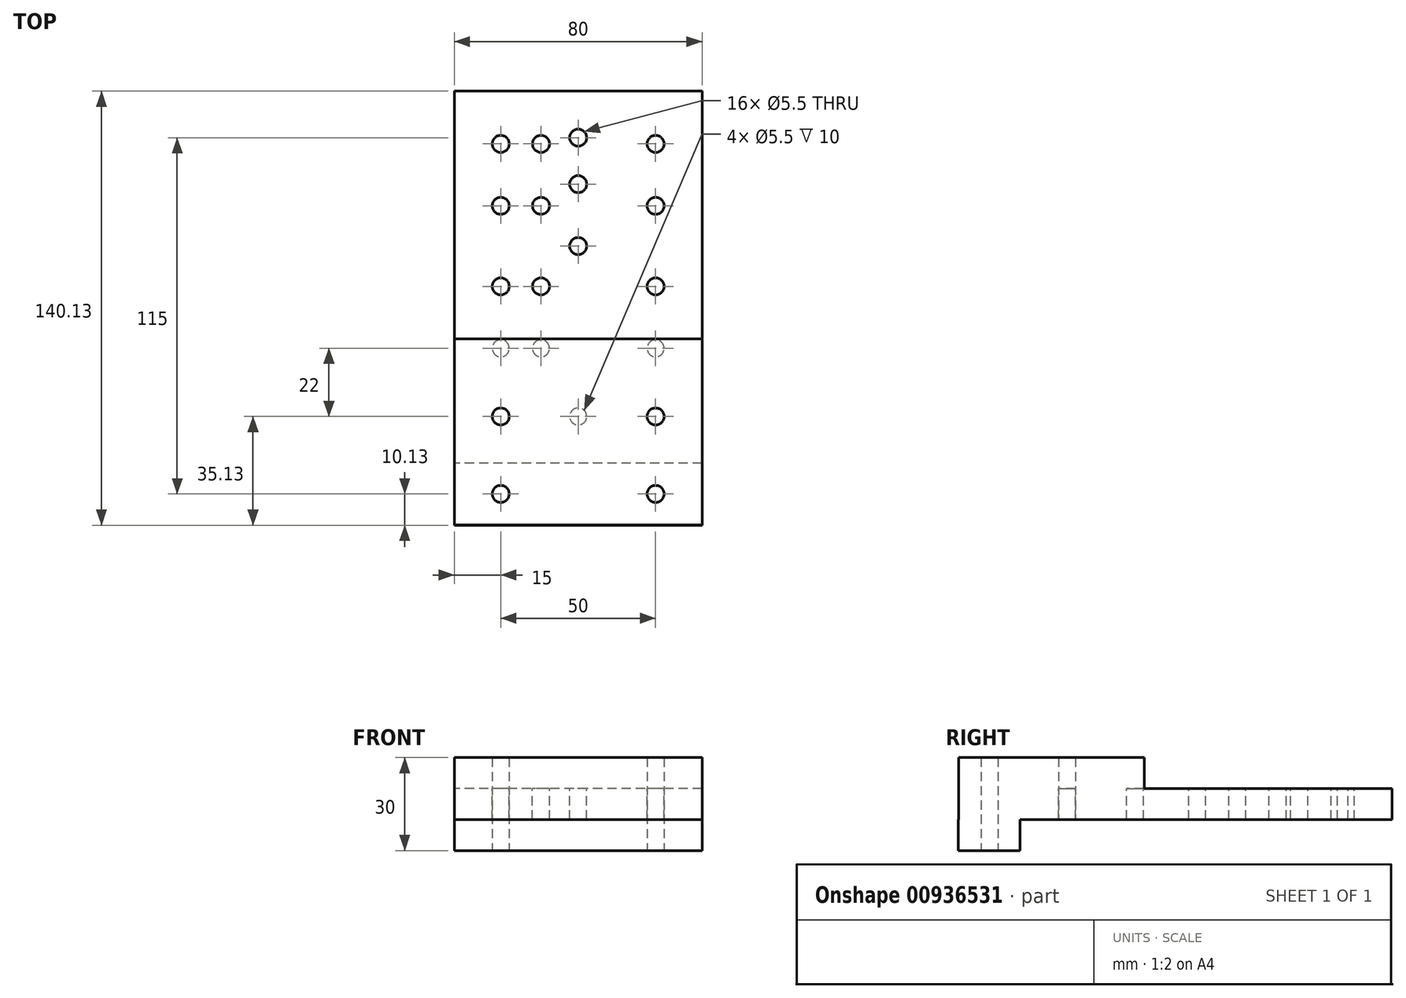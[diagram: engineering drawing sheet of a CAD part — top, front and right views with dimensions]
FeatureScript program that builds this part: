
annotation { "Feature Type Name" : "Feature", "Feature Type Description" : "" }
export const myFeature = defineFeature(function(context is Context, id is Id, definition is map)
    precondition{}
    {
        {
            var Q0;
            Q0=qCreatedBy(makeId("Top.planeOp"),FACE);
            var sketch = newSketch(context, id + "F0", { "sketchPlane" : qUnion([Q0])});
            skLineSegment(sketch, "E0.bottom", {"start": v(40, 70) * mm, "end": v(-40, 70) * mm});
            skLineSegment(sketch, "E0.top", {"start": v(40, -70) * mm, "end": v(-40, -70) * mm});
            skLineSegment(sketch, "E0.left", {"start": v(40, 70) * mm, "end": v(40, -70) * mm});
            skLineSegment(sketch, "E0.right", {"start": v(-40, 70) * mm, "end": v(-40, -70) * mm});
            skPoint(sketch, "E0.middle", {"position": v(0, 0) * mm});
            skLineSegment(sketch, "E1", {"start": v(-40, 30) * mm, "end": v(40, 30) * mm, "construction": true});
            skLineSegment(sketch, "E2", {"start": v(-40, 10) * mm, "end": v(40, 10) * mm, "construction": true});
            skPoint(sketch, "E3", {"position": v(-25, 53) * mm});
            skPoint(sketch, "E4", {"position": v(-12, 53) * mm});
            skPoint(sketch, "E5", {"position": v(25, 53) * mm});
            skPoint(sketch, "E6.MirrorP", {"position": v(-25, 7) * mm});
            skPoint(sketch, "E7.MirrorP", {"position": v(-12, 7) * mm});
            skPoint(sketch, "E8.MirrorP", {"position": v(25, 7) * mm});
            skPoint(sketch, "E9", {"position": v(-25, 33) * mm});
            skPoint(sketch, "E10", {"position": v(-12, 33) * mm});
            skPoint(sketch, "E11", {"position": v(25, 33) * mm});
            skPoint(sketch, "E12.MirrorP", {"position": v(-25, -13) * mm});
            skPoint(sketch, "E13.MirrorP", {"position": v(-12, -13) * mm});
            skPoint(sketch, "E14.MirrorP", {"position": v(25, -13) * mm});
            skPoint(sketch, "E15", {"position": v(0, -35) * mm});
            skPoint(sketch, "E16.MirrorP", {"position": v(0, 55) * mm});
            skPoint(sketch, "E17", {"position": v(0, 40) * mm});
            skPoint(sketch, "E18.MirrorP", {"position": v(0, 20) * mm});
            skSolve(sketch);
        }
        {
            var Q0;
            Q0 = qSketchRegion(id + "F0", true);
            extrude(context, id + "F1", {"entities" : qUnion([Q0]), "depth" : 10 * mm, "offsetDistance" : 25 * mm});
        }
        {
            var Q0;
            Q0=sQuery(id+"F0.wireOp",VERTEX,"E8.MirrorP");
            var Q1;
            Q1=sQuery(id+"F0.wireOp",VERTEX,"E14.MirrorP");
            var Q2;
            Q2=sQuery(id+"F0.wireOp",VERTEX,"E11");
            var Q3;
            Q3=sQuery(id+"F0.wireOp",VERTEX,"E5");
            var Q4;
            Q4=sQuery(id+"F0.wireOp",VERTEX,"E4");
            var Q5;
            Q5=sQuery(id+"F0.wireOp",VERTEX,"E10");
            var Q6;
            Q6=sQuery(id+"F0.wireOp",VERTEX,"E9");
            var Q7;
            Q7=sQuery(id+"F0.wireOp",VERTEX,"E3");
            var Q8;
            Q8=sQuery(id+"F0.wireOp",VERTEX,"E7.MirrorP");
            var Q9;
            Q9=sQuery(id+"F0.wireOp",VERTEX,"E6.MirrorP");
            var Q10;
            Q10=sQuery(id+"F0.wireOp",VERTEX,"E13.MirrorP");
            var Q11;
            Q11=sQuery(id+"F0.wireOp",VERTEX,"E12.MirrorP");
            var Q12;
            Q12=makeQuery(id+"F1.opExtrude","SWEPT_BODY",BODY,{"disambiguationData":[OSD([sQuery(id+"F0.wireOp",EDGE,"E0.bottom"),sQuery(id+"F0.wireOp",EDGE,"E0.top"),sQuery(id+"F0.wireOp",EDGE,"E0.left"),sQuery(id+"F0.wireOp",EDGE,"E0.right")])]});
            hole(context, id + "F2", {"style" : HoleStyle.SIMPLE, "endStyle" : HoleEndStyle.THROUGH, "oppositeDirection" : true, "standardTappedOrClearance" : lookupTablePath({ "fit" : "Normal", "standard" : "ISO", "size" : "M5", "type" : "Clearance" }), "standardBlindInLast" : lookupTablePath({ "fit" : "Normal", "standard" : "ISO", "engagement" : "75%", "pitch" : "0.8 mm", "size" : "M5", "type" : "Clearance & tapped" }), "holeDiameter" : 5.5 * mm, "majorDiameter" : 5 * mm, "tappedDepth" : 12 * mm, "tapClearance" : 3, "locations" : qUnion([Q0, Q1, Q2, Q3, Q4, Q5, Q6, Q7, Q8, Q9, Q10, Q11]), "scope" : qUnion([Q12]), "startStyle" : HoleStartStyle.PART});
        }
        {
            var Q0;
            Q0=sQuery(id+"F0.wireOp",VERTEX,"E17");
            var Q1;
            Q1=sQuery(id+"F0.wireOp",VERTEX,"E16.MirrorP");
            var Q2;
            Q2=sQuery(id+"F0.wireOp",VERTEX,"E15");
            var Q3;
            Q3=sQuery(id+"F0.wireOp",VERTEX,"E18.MirrorP");
            var Q4;
            Q4=makeQuery(id+"F1.opExtrude","SWEPT_BODY",BODY,{"disambiguationData":[OSD([sQuery(id+"F0.wireOp",EDGE,"E0.bottom"),sQuery(id+"F0.wireOp",EDGE,"E0.top"),sQuery(id+"F0.wireOp",EDGE,"E0.left"),sQuery(id+"F0.wireOp",EDGE,"E0.right")])]});
            hole(context, id + "F3", {"style" : HoleStyle.SIMPLE, "endStyle" : HoleEndStyle.THROUGH, "oppositeDirection" : true, "standardTappedOrClearance" : lookupTablePath({ "fit" : "Normal", "standard" : "ISO", "size" : "M5", "type" : "Clearance" }), "standardBlindInLast" : lookupTablePath({ "fit" : "Normal", "standard" : "ISO", "engagement" : "75%", "pitch" : "0.8 mm", "size" : "M5", "type" : "Clearance & tapped" }), "holeDiameter" : 5.5 * mm, "majorDiameter" : 5 * mm, "tappedDepth" : 12 * mm, "tapClearance" : 3, "locations" : qUnion([Q0, Q1, Q2, Q3]), "scope" : qUnion([Q4]), "startStyle" : HoleStartStyle.PART});
        }
        {
            var Q0;
            Q0=makeQuery(id+"F0.imprint","IMPRINT",FACE,{"disambiguationData":[TD([[makeQuery(id+"F0.imprint","IMPRINT",EDGE,{"derivedFrom":sQuery(id+"F0.wireOp",EDGE,"E0.bottom")}),1.0]])]});
            var sketch = newSketch(context, id + "F4", { "sketchPlane" : qUnion([Q0])});
            skLineSegment(sketch, "E19.bottom", {"start": v(40, -70.13) * mm, "end": v(-40, -70.13) * mm});
            skLineSegment(sketch, "E19.top", {"start": v(40, -50.13) * mm, "end": v(-40, -50.13) * mm});
            skLineSegment(sketch, "E19.left", {"start": v(40, -70.13) * mm, "end": v(40, -50.13) * mm});
            skLineSegment(sketch, "E19.right", {"start": v(-40, -70.13) * mm, "end": v(-40, -50.13) * mm});
            skPoint(sketch, "E19.middle", {"position": v(0, -60.13) * mm});
            skSolve(sketch);
        }
        {
            var Q0;
            Q0 = qSketchRegion(id + "F4", true);
            extrude(context, id + "F5", {"entities" : qUnion([Q0]), "operationType" : NewBodyOperationType.ADD, "oppositeDirection" : true, "depth" : 10 * mm, "offsetDistance" : 25 * mm});
        }
        {
            var Q0;
            Q0=makeQuery(id+"F1.opExtrude","CAP_FACE",FACE,{"disambiguationData":[OSD([sQuery(id+"F0.wireOp",EDGE,"E0.bottom"),sQuery(id+"F0.wireOp",EDGE,"E0.top"),sQuery(id+"F0.wireOp",EDGE,"E0.left"),sQuery(id+"F0.wireOp",EDGE,"E0.right")])],"isStart":false});
            var sketch = newSketch(context, id + "F6", { "sketchPlane" : qUnion([Q0])});
            skLineSegment(sketch, "E20.bottom", {"start": v(40, -70) * mm, "end": v(-40, -70) * mm});
            skLineSegment(sketch, "E20.top", {"start": v(40, -10) * mm, "end": v(-40, -10) * mm});
            skLineSegment(sketch, "E20.left", {"start": v(40, -70) * mm, "end": v(40, -10) * mm});
            skLineSegment(sketch, "E20.right", {"start": v(-40, -70) * mm, "end": v(-40, -10) * mm});
            skPoint(sketch, "E20.middle", {"position": v(0, -40) * mm});
            skSolve(sketch);
        }
        {
            var Q0;
            Q0 = qSketchRegion(id + "F6", true);
            extrude(context, id + "F7", {"entities" : qUnion([Q0]), "operationType" : NewBodyOperationType.ADD, "depth" : 10 * mm, "offsetDistance" : 25 * mm});
        }
        {
            var Q0;
            Q0=makeQuery(id+"F7.opExtrude","CAP_FACE",FACE,{"disambiguationData":[OSD([sQuery(id+"F6.wireOp",EDGE,"E20.bottom"),sQuery(id+"F6.wireOp",EDGE,"E20.top"),sQuery(id+"F6.wireOp",EDGE,"E20.left"),sQuery(id+"F6.wireOp",EDGE,"E20.right")])],"isStart":false});
            var sketch = newSketch(context, id + "F8", { "sketchPlane" : qUnion([Q0])});
            skPoint(sketch, "E21", {"position": v(-25, -35) * mm});
            skPoint(sketch, "E22.MirrorP", {"position": v(25, -35) * mm});
            skPoint(sketch, "E23", {"position": v(-25, -60) * mm});
            skPoint(sketch, "E24.MirrorP", {"position": v(25, -60) * mm});
            skSolve(sketch);
        }
        {
            var Q0;
            Q0=sQuery(id+"F8.wireOp",VERTEX,"E21");
            var Q1;
            Q1=sQuery(id+"F8.wireOp",VERTEX,"E22.MirrorP");
            var Q2;
            Q2=sQuery(id+"F8.wireOp",VERTEX,"E23");
            var Q3;
            Q3=sQuery(id+"F8.wireOp",VERTEX,"E24.MirrorP");
            var Q4;
            Q4=makeQuery(id+"F1.opExtrude","SWEPT_BODY",BODY,{"disambiguationData":[OSD([sQuery(id+"F0.wireOp",EDGE,"E0.bottom"),sQuery(id+"F0.wireOp",EDGE,"E0.top"),sQuery(id+"F0.wireOp",EDGE,"E0.left"),sQuery(id+"F0.wireOp",EDGE,"E0.right")])]});
            hole(context, id + "F9", {"style" : HoleStyle.SIMPLE, "endStyle" : HoleEndStyle.THROUGH, "standardTappedOrClearance" : lookupTablePath({ "fit" : "Normal", "standard" : "ISO", "size" : "M5", "type" : "Clearance" }), "standardBlindInLast" : lookupTablePath({ "fit" : "Normal", "standard" : "ISO", "engagement" : "75%", "pitch" : "0.8 mm", "size" : "M5", "type" : "Clearance & tapped" }), "holeDiameter" : 5.5 * mm, "majorDiameter" : 5 * mm, "tappedDepth" : 12 * mm, "tapClearance" : 3, "locations" : qUnion([Q0, Q1, Q2, Q3]), "scope" : qUnion([Q4]), "startStyle" : HoleStartStyle.PART});
        }
    });
